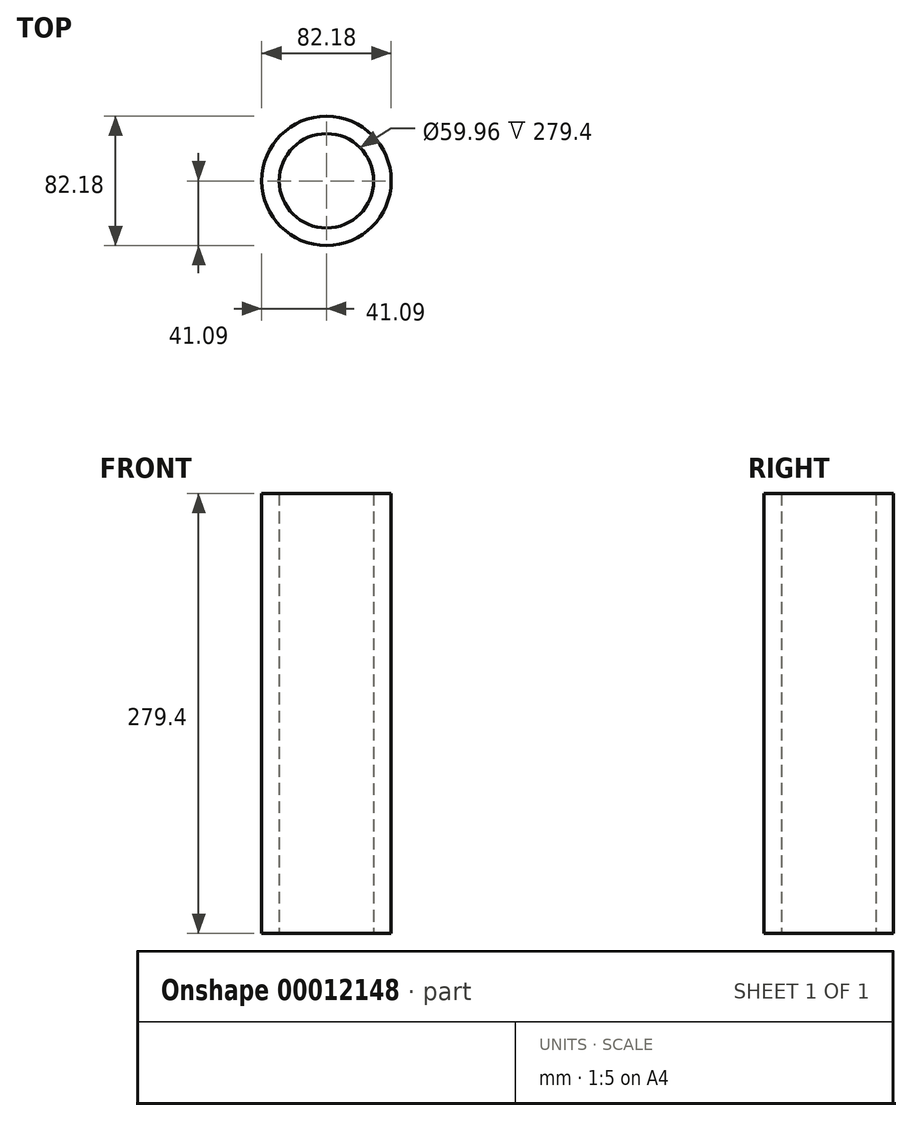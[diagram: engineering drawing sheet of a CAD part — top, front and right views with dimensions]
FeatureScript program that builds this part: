
annotation { "Feature Type Name" : "Feature", "Feature Type Description" : "" }
export const myFeature = defineFeature(function(context is Context, id is Id, definition is map)
    precondition{}
    {
        {
            var Q0;
            Q0=qCreatedBy(makeId("Top.planeOp"),FACE);
            var sketch = newSketch(context, id + "F0", { "sketchPlane" : qUnion([Q0])});
            skCircle(sketch, "E0", {"center": v(0, 0) * mm, "radius": 41.1 * mm});
            skCircle(sketch, "E1", {"center": v(0, 0) * mm, "radius": 29.98 * mm});
            skSolve(sketch);
        }
        {
            var Q0;
            Q0=makeQuery(id+"F0.imprint","IMPRINT",FACE,{"disambiguationData":[TD([[makeQuery(id+"F0.imprint","IMPRINT",EDGE,{"derivedFrom":sQuery(id+"F0.wireOp",EDGE,"E0")}),1.0]])]});
            extrude(context, id + "F1", {"entities" : qUnion([Q0]), "flatOperationType" : FlatOperationType.REMOVE, "depth" : 279.4 * mm, "offsetDistance" : 25.4 * mm, "domain" : OperationDomain.MODEL});
        }
    });
